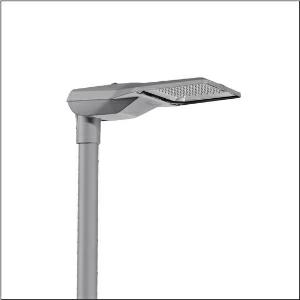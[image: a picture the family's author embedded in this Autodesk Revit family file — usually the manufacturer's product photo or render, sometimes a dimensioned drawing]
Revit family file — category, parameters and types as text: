
# Revit family: streetlight_sl_21_midi___stw1_0a_5xe3e43s08lb_9506
name_source: partatom
category: Lighting Fixtures
units: mm (PartAtom-declared; Revit-internal decimal feet)

## family parameters
Cut with Voids When Loaded = No
Host = Face
Light Source = No
Part Type = Normal
Room Calculation Point = No
Round Connector Dimension = Use Diameter
Shared = No

## types (1)
- --- (1 x LED, 14950 lm, 98.3 W, 4000K)
    Apparent Load = 98 VA
    CIE Flux Codes = 38 75 98 100 100
    Color Rendering = 70
    Color Temperature = 4000K
    Default Elevation = 1800 mm
    Description = Streetlight SL 21 midi, mast luminaire, primary light control with lens, of PMMA, primary optical cover: cover, of toughened safety glass, transparent, light distribution: STW1.0a, light emission: direct distribution, primary light characteristic: asymmetric, installation type: side-entry, post-top, LED, High Power LED, rated luminous flux: 14.950lm, luminous efficacy: 152lm/W, light colour: 740, colour temperature: 4000K, control: overheat protection, constant luminous flux control, time-dependent luminous flux control, flexible luminous flux parameterisation, presetting dimming logarithmic, mains connection: 230..240V, AC, 50/60Hz, start of lifetime: 98W, end of service life: 101W, reduction: 45W, luminaire housing, of diecast aluminium, powder-coated, Siteco® metallic grey (DB 702S), corrosivity category C5 mid according to DIN EN ISO 12944, please order mast flange separately, inclination adjustable: 0°, 5°, 10°, 15°, sealing non-destructively replaceable, multi-level sealing system, length: 644mm, width: 335mm, height: 110mm, mast flange for spigot size: 42mm (side-entry): 5XC10008XM4, 60/48mm (side-entry/post-top): 5XC10108XM2, 76/60mm (side-entry/post-top): 5XC10108XM1, Smart Interface above, protection rating (complete): IP66, insulation class (complete): insulation class II (safety insulation), certification: CE, ENEC, ENEC+, VDE, impact resistance: IK09, permissible operating ambient temperature for outdoor applications: -40..+50°C, standard-compliant lighting for roads and squares, packaging unit: 1 piece

Light Distribution: STW1.0a
    Height = 111 mm
    Lamp = 1 x LED
    Lamp Light Flux = 14950 lm
    Lamp Power = 98.3 W
    Lamp count = 1
    Length = 644 mm
    Luminous efficacy = 152 lm/W
    Manufacturer = Siteco
    ModVariant = No
    Model = 5XE3E43S08LB
    Number of Poles = 1
    OnlyDefault = Yes
    Power Factor = 1
    Product Name = Streetlight SL 21 midi | STW1.0a
    Product group = mast luminaire | pylon top
    ProductGroupID = 6100
    Protection Class = Protection class II
    Protection Degree = IP 66
    RLX_Detail_Level = 1
    RLX_Emergency_Light_Flux = 0 lm
    RLX_Emergency_Type = 0
    RLX_Emergency_Type_DB = No
    RlxData = <blob elided: 90737 chars, md5=63e28a44>
    Socket = socket
    Standby Power = 0 W
    System Light Flux = 14950 lm
    System Power = 98 W
    Type Comments = factory setting: luminous flux: 100 % | dim-lin: 254 | 1020 mA
    Type Image = l_1004302.jpg
    URL = http://relux.com
    VarID = @adj_121673
    Voltage = 0 V
    Weight = 0.00 kg
    Width = 336 mm

## geometry (parser evidence)
native form markers: Blend x4, Sweep x10
no freeform markers — native parametric forms only
